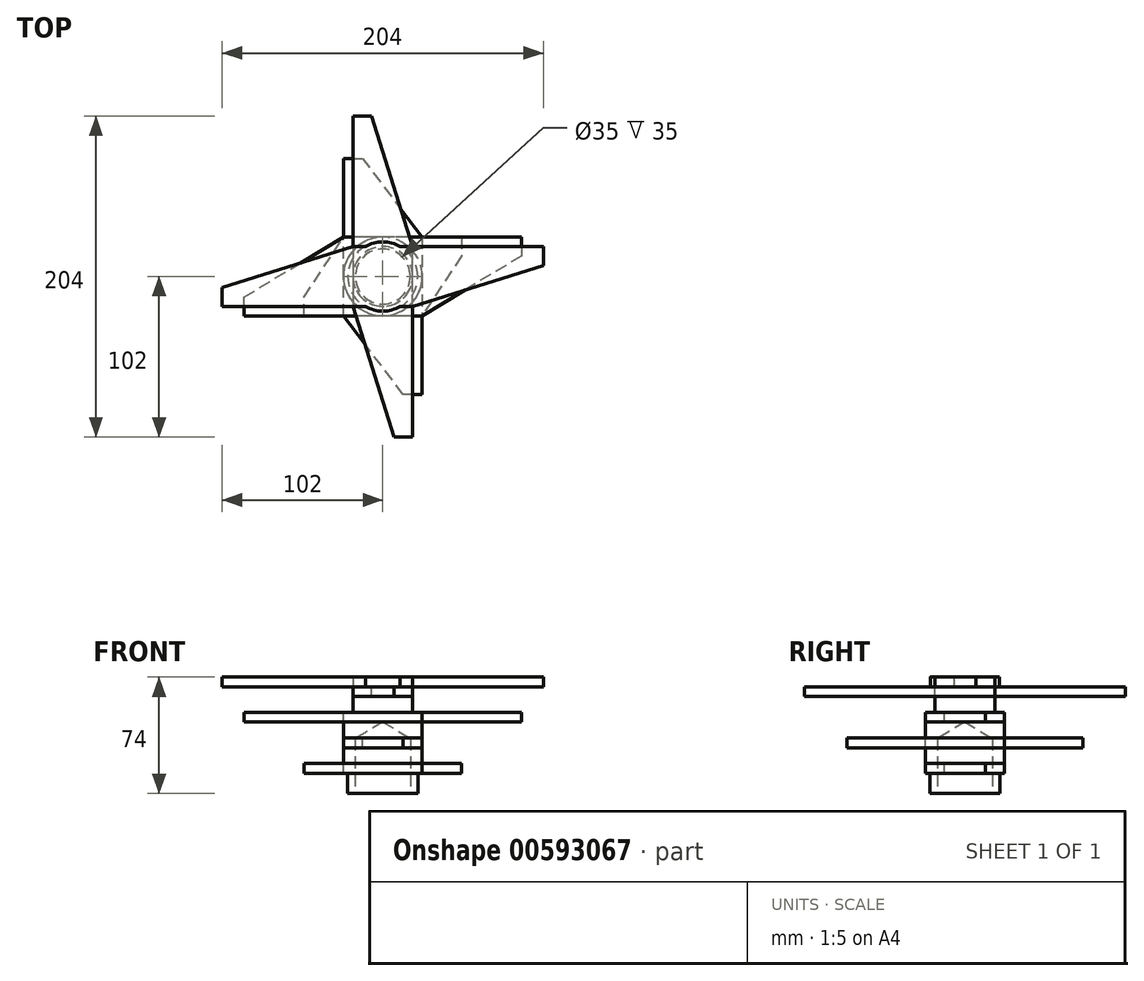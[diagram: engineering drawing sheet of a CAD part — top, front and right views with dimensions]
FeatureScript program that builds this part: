
annotation { "Feature Type Name" : "Feature", "Feature Type Description" : "" }
export const myFeature = defineFeature(function(context is Context, id is Id, definition is map)
    precondition{}
    {
        {
            var Q0;
            Q0=qCreatedBy(makeId("Top.planeOp"),FACE);
            var sketch = newSketch(context, id + "F0", { "sketchPlane" : qUnion([Q0])});
            skArc(sketch, "E0", {"start": v(11.1, 19) * mm, "mid": v(0, 22) * mm, "end": v(-11.1, 19) * mm});
            skLineSegment(sketch, "E1.bottom", {"start": v(19, -19) * mm, "end": v(11.1, -19) * mm});
            skLineSegment(sketch, "E2", {"start": v(102, 19) * mm, "end": v(102, 7) * mm});
            skLineSegment(sketch, "E3", {"start": v(102, 7) * mm, "end": v(19, -19) * mm});
            skLineSegment(sketch, "E4", {"start": v(-102, -19) * mm, "end": v(-102, -7) * mm});
            skLineSegment(sketch, "E5", {"start": v(-102, -7) * mm, "end": v(-19, 19) * mm});
            skLineSegment(sketch, "E6", {"start": v(-102, -19) * mm, "end": v(-11.1, -19) * mm});
            skLineSegment(sketch, "E7", {"start": v(11.1, -19) * mm, "end": v(19, -19) * mm});
            skLineSegment(sketch, "E8", {"start": v(-11.1, 19) * mm, "end": v(-19, 19) * mm});
            skPoint(sketch, "E9.orphan", {"position": v(0, 19) * mm});
            skArc(sketch, "E10.trimOffspring", {"start": v(-11.1, -19) * mm, "mid": v(0, -22) * mm, "end": v(11.1, -19) * mm});
            skPoint(sketch, "E11.orphan", {"position": v(0, -19) * mm});
            skLineSegment(sketch, "E12", {"start": v(11.1, 19) * mm, "end": v(102, 19) * mm});
            skSolve(sketch);
        }
        {
            var Q0;
            Q0=makeQuery(id+"F0.imprint","IMPRINT",FACE,{"disambiguationData":[TD([[makeQuery(id+"F0.imprint","IMPRINT",EDGE,{"derivedFrom":sQuery(id+"F0.wireOp",EDGE,"E0")}),1.0]])]});
            extrude(context, id + "F1", {"entities" : qUnion([Q0]), "depth" : 6.2 * mm, "offsetDistance" : 25 * mm});
        }
        {
            var Q0;
            Q0=makeQuery(id+"F1.opExtrude","CAP_FACE",FACE,{"disambiguationData":[OSD([sQuery(id+"F0.wireOp",EDGE,"E0"),sQuery(id+"F0.wireOp",EDGE,"E2"),sQuery(id+"F0.wireOp",EDGE,"E3"),sQuery(id+"F0.wireOp",EDGE,"E4"),sQuery(id+"F0.wireOp",EDGE,"E5"),sQuery(id+"F0.wireOp",EDGE,"E6"),sQuery(id+"F0.wireOp",EDGE,"E7"),sQuery(id+"F0.wireOp",EDGE,"E8"),sQuery(id+"F0.wireOp",EDGE,"E10.trimOffspring"),sQuery(id+"F0.wireOp",EDGE,"E12")])],"isStart":true});
            var sketch = newSketch(context, id + "F2", { "sketchPlane" : qUnion([Q0])});
            skLineSegment(sketch, "E13", {"start": v(-19, 0) * mm, "end": v(-19, 19) * mm});
            skLineSegment(sketch, "E14", {"start": v(19, 102) * mm, "end": v(19, 0) * mm});
            skLineSegment(sketch, "E15", {"start": v(19, 0) * mm, "end": v(19, -19) * mm});
            skLineSegment(sketch, "E16", {"start": v(-19, -102) * mm, "end": v(-19, 0) * mm});
            skLineSegment(sketch, "E17", {"start": v(19, 102) * mm, "end": v(7, 102) * mm});
            skLineSegment(sketch, "E18", {"start": v(7, 102) * mm, "end": v(-19, 19) * mm});
            skLineSegment(sketch, "E19", {"start": v(-19, -102) * mm, "end": v(-7, -102) * mm});
            skLineSegment(sketch, "E20", {"start": v(-7, -102) * mm, "end": v(19, -19) * mm});
            skSolve(sketch);
        }
        {
            var Q0;
            {var subQ5=sQuery(id+"F2.wireOp",EDGE,"E13");Q0=makeQuery(id+"F2.imprint","IMPRINT",FACE,{"disambiguationData":[TD([[makeQuery(id+"F2.imprint","IMPRINT",EDGE,{"derivedFrom":subQ5}),-1.0]])]});}
            var Q1;
            {var subQ3=sQuery(id+"F2.wireOp",EDGE,"E19");Q1=makeQuery(id+"F2.imprint","IMPRINT",FACE,{"disambiguationData":[TD([[makeQuery(id+"F2.imprint","IMPRINT",EDGE,{"derivedFrom":subQ3}),1.0]])]});}
            var Q2;
            {var subQ2=sQuery(id+"F2.wireOp",EDGE,"E17");Q2=makeQuery(id+"F2.imprint","IMPRINT",FACE,{"disambiguationData":[TD([[makeQuery(id+"F2.imprint","IMPRINT",EDGE,{"derivedFrom":subQ2}),1.0]])]});}
            extrude(context, id + "F3", {"entities" : qUnion([Q0, Q1, Q2]), "operationType" : NewBodyOperationType.ADD, "depth" : 6.2 * mm, "offsetDistance" : 25 * mm});
        }
        {
            var Q0;
            Q0=makeQuery(id+"F3.opExtrude","CAP_FACE",FACE,{"disambiguationData":[OSD([sQuery(id+"F2.wireOp",EDGE,"E13"),sQuery(id+"F2.wireOp",EDGE,"E14"),sQuery(id+"F2.wireOp",EDGE,"E15"),sQuery(id+"F2.wireOp",EDGE,"E16"),sQuery(id+"F2.wireOp",EDGE,"E17"),sQuery(id+"F2.wireOp",EDGE,"E18"),sQuery(id+"F2.wireOp",EDGE,"E19"),sQuery(id+"F2.wireOp",EDGE,"E20")])],"isStart":false});
            var sketch = newSketch(context, id + "F4", { "sketchPlane" : qUnion([Q0])});
            skCircle(sketch, "E21", {"center": v(0, 0) * mm, "radius": 19 * mm});
            skSolve(sketch);
        }
        {
            var Q0;
            {var subQ0=sQuery(id+"F4.wireOp",EDGE,"E21");var subQ3=makeQuery(id+"F3.opExtrude","CAP_EDGE",EDGE,{"disambiguationData":[OSD([sQuery(id+"F2.wireOp",EDGE,"E20")])],"isStart":false});var subQ4=makeQuery(id+"F4.imprint","INTERSECT",VERTEX,{"derivedFrom":[subQ3,subQ0]});Q0=makeQuery(id+"F4.imprint","IMPRINT",FACE,{"disambiguationData":[TD([[makeQuery(id+"F4.imprint","IMPRINT",EDGE,{"disambiguationData":[TD([[subQ4,-1.0]])],"derivedFrom":subQ0}),1.0]])]});}
            var Q1;
            {var subQ3=sQuery(id+"F4.wireOp",EDGE,"E21");var subQ5=makeQuery(id+"F3.opExtrude","CAP_EDGE",EDGE,{"disambiguationData":[OSD([sQuery(id+"F2.wireOp",EDGE,"E18")])],"isStart":false});var subQ10=makeQuery(id+"F4.imprint","INTERSECT",VERTEX,{"derivedFrom":[subQ5,subQ3]});Q1=makeQuery(id+"F4.imprint","IMPRINT",FACE,{"disambiguationData":[TD([[makeQuery(id+"F4.imprint","IMPRINT",EDGE,{"disambiguationData":[TD([[subQ10,1.0]])],"derivedFrom":subQ3}),1.0]])]});}
            var Q2;
            {var subQ0=sQuery(id+"F4.wireOp",EDGE,"E21");var subQ1=makeQuery(id+"F3.opExtrude","CAP_EDGE",EDGE,{"disambiguationData":[OSD([sQuery(id+"F2.wireOp",EDGE,"E18")])],"isStart":false});var subQ2=makeQuery(id+"F4.imprint","INTERSECT",VERTEX,{"derivedFrom":[subQ1,subQ0]});Q2=makeQuery(id+"F4.imprint","IMPRINT",FACE,{"disambiguationData":[TD([[makeQuery(id+"F4.imprint","IMPRINT",EDGE,{"disambiguationData":[TD([[subQ2,-1.0]])],"derivedFrom":subQ0}),1.0]])]});}
            extrude(context, id + "F5", {"entities" : qUnion([Q0, Q1, Q2]), "operationType" : NewBodyOperationType.ADD, "depth" : 10 * mm, "offsetDistance" : 25 * mm});
        }
        {
            var Q0;
            Q0=makeQuery(id+"F5.opExtrude","CAP_FACE",FACE,{"disambiguationData":[OSD([sQuery(id+"F4.wireOp",EDGE,"E21")])],"isStart":false});
            var sketch = newSketch(context, id + "F6", { "sketchPlane" : qUnion([Q0])});
            skLineSegment(sketch, "E22.bottom", {"start": v(25, -25) * mm, "end": v(-25, -25) * mm});
            skLineSegment(sketch, "E22.top", {"start": v(25, 25) * mm, "end": v(-25, 25) * mm});
            skLineSegment(sketch, "E22.left", {"start": v(25, -25) * mm, "end": v(25, 25) * mm});
            skLineSegment(sketch, "E22.right", {"start": v(-25, -25) * mm, "end": v(-25, 25) * mm});
            skPoint(sketch, "E22.middle", {"position": v(0, 0) * mm});
            skLineSegment(sketch, "E23", {"start": v(25, -25) * mm, "end": v(88, -25) * mm});
            skLineSegment(sketch, "E24", {"start": v(88, -25) * mm, "end": v(88, -13) * mm});
            skLineSegment(sketch, "E25", {"start": v(88, -13) * mm, "end": v(25, 25) * mm});
            skLineSegment(sketch, "E26", {"start": v(-25, 25) * mm, "end": v(-88, 25) * mm});
            skLineSegment(sketch, "E27", {"start": v(-88, 25) * mm, "end": v(-88, 13) * mm});
            skLineSegment(sketch, "E28", {"start": v(-88, 13) * mm, "end": v(-25, -25) * mm});
            skSolve(sketch);
        }
        {
            var Q0;
            Q0=makeQuery(id+"F6.imprint","IMPRINT",FACE,{"disambiguationData":[TD([[makeQuery(id+"F6.imprint","IMPRINT",EDGE,{"derivedFrom":sQuery(id+"F6.wireOp",EDGE,"E22.bottom")}),-1.0]])]});
            var Q1;
            Q1=makeQuery(id+"F6.imprint","IMPRINT",FACE,{"disambiguationData":[TD([[makeQuery(id+"F6.imprint","IMPRINT",EDGE,{"derivedFrom":sQuery(id+"F6.wireOp",EDGE,"E22.left")}),-1.0]])]});
            var Q2;
            Q2=makeQuery(id+"F6.imprint","IMPRINT",FACE,{"disambiguationData":[TD([[makeQuery(id+"F6.imprint","IMPRINT",EDGE,{"derivedFrom":sQuery(id+"F6.wireOp",EDGE,"E22.right")}),1.0]])]});
            var Q3;
            Q3=makeQuery(id+"F6.imprint","IMPRINT",FACE,{"disambiguationData":[TD([[makeQuery(id+"F6.imprint","IMPRINT",EDGE,{"derivedFrom":makeQuery(id+"F5.opExtrude","CAP_EDGE",EDGE,{"disambiguationData":[OSD([sQuery(id+"F4.wireOp",EDGE,"E21")])],"isStart":false})}),1.0]])]});
            extrude(context, id + "F7", {"entities" : qUnion([Q0, Q1, Q2, Q3]), "operationType" : NewBodyOperationType.ADD, "depth" : 6.2 * mm, "offsetDistance" : 25 * mm});
        }
        {
            var Q0;
            Q0=makeQuery(id+"F7.opExtrude","CAP_FACE",FACE,{"disambiguationData":[OSD([sQuery(id+"F6.wireOp",EDGE,"E22.bottom"),sQuery(id+"F6.wireOp",EDGE,"E22.top"),sQuery(id+"F6.wireOp",EDGE,"E23"),sQuery(id+"F6.wireOp",EDGE,"E24"),sQuery(id+"F6.wireOp",EDGE,"E25"),sQuery(id+"F6.wireOp",EDGE,"E26"),sQuery(id+"F6.wireOp",EDGE,"E27"),sQuery(id+"F6.wireOp",EDGE,"E28")])],"isStart":false});
            var sketch = newSketch(context, id + "F8", { "sketchPlane" : qUnion([Q0])});
            skCircle(sketch, "E29", {"center": v(0, 0) * mm, "radius": 25 * mm});
            skSolve(sketch);
        }
        {
            var Q0;
            {var subQ0=sQuery(id+"F8.wireOp",EDGE,"E29");var subQ1=makeQuery(id+"F8.imprint","INTERSECT",VERTEX,{"derivedFrom":[makeQuery(id+"F7.opExtrude","CAP_EDGE",EDGE,{"disambiguationData":[OSD([sQuery(id+"F6.wireOp",EDGE,"E22.bottom"),sQuery(id+"F6.wireOp",EDGE,"E23")])],"isStart":false}),subQ0]});Q0=makeQuery(id+"F8.imprint","IMPRINT",FACE,{"disambiguationData":[TD([[makeQuery(id+"F8.imprint","IMPRINT",EDGE,{"disambiguationData":[TD([[subQ1,1.0]])],"derivedFrom":subQ0}),1.0]])]});}
            extrude(context, id + "F9", {"entities" : qUnion([Q0]), "operationType" : NewBodyOperationType.ADD, "depth" : 10 * mm, "offsetDistance" : 25 * mm});
        }
        {
            var Q0;
            Q0=makeQuery(id+"F9.opExtrude","CAP_FACE",FACE,{"disambiguationData":[OSD([sQuery(id+"F8.wireOp",EDGE,"E29")])],"isStart":false});
            var sketch = newSketch(context, id + "F10", { "sketchPlane" : qUnion([Q0])});
            skLineSegment(sketch, "E30.bottom", {"start": v(-25, -25) * mm, "end": v(25, -25) * mm});
            skLineSegment(sketch, "E30.top", {"start": v(-25, 25) * mm, "end": v(25, 25) * mm});
            skLineSegment(sketch, "E30.left", {"start": v(-25, -25) * mm, "end": v(-25, 25) * mm});
            skLineSegment(sketch, "E30.right", {"start": v(25, -25) * mm, "end": v(25, 25) * mm});
            skPoint(sketch, "E30.middle", {"position": v(0, 0) * mm});
            skLineSegment(sketch, "E31", {"start": v(25, 25) * mm, "end": v(25, 75) * mm});
            skLineSegment(sketch, "E32", {"start": v(25, 75) * mm, "end": v(13, 75) * mm});
            skLineSegment(sketch, "E33", {"start": v(13, 75) * mm, "end": v(-25, 25) * mm});
            skLineSegment(sketch, "E34", {"start": v(-25, -75) * mm, "end": v(-13, -75) * mm});
            skLineSegment(sketch, "E35", {"start": v(-13, -75) * mm, "end": v(25, -25) * mm});
            skLineSegment(sketch, "E36", {"start": v(-25, -25) * mm, "end": v(-25, -75) * mm});
            skSolve(sketch);
        }
        {
            var Q0;
            {var subQ0=sQuery(id+"F10.wireOp",EDGE,"E31");Q0=makeQuery(id+"F10.imprint","IMPRINT",FACE,{"disambiguationData":[TD([[makeQuery(id+"F10.imprint","IMPRINT",EDGE,{"derivedFrom":subQ0}),1.0]])]});}
            var Q1;
            {var subQ0=sQuery(id+"F10.wireOp",EDGE,"E30.right");var subQ3=makeQuery(id+"F9.opExtrude","CAP_EDGE",EDGE,{"disambiguationData":[OSD([sQuery(id+"F8.wireOp",EDGE,"E29")])],"isStart":false});var subQ5=makeQuery(id+"F10.imprint","INTERSECT",VERTEX,{"derivedFrom":[subQ3,subQ0]});Q1=makeQuery(id+"F10.imprint","IMPRINT",FACE,{"disambiguationData":[TD([[makeQuery(id+"F10.imprint","IMPRINT",EDGE,{"disambiguationData":[TD([[subQ5,-1.0]])],"derivedFrom":subQ3}),-1.0]])]});}
            var Q2;
            {var subQ0=makeQuery(id+"F9.opExtrude","CAP_EDGE",EDGE,{"disambiguationData":[OSD([sQuery(id+"F8.wireOp",EDGE,"E29")])],"isStart":false});var subQ1=makeQuery(id+"F10.imprint","INTERSECT",VERTEX,{"derivedFrom":[subQ0,sQuery(id+"F10.wireOp",EDGE,"E30.left")]});Q2=makeQuery(id+"F10.imprint","IMPRINT",FACE,{"disambiguationData":[TD([[makeQuery(id+"F10.imprint","IMPRINT",EDGE,{"disambiguationData":[TD([[subQ1,-1.0]])],"derivedFrom":subQ0}),1.0]])]});}
            var Q3;
            {var subQ0=sQuery(id+"F10.wireOp",EDGE,"E30.right");var subQ3=makeQuery(id+"F9.opExtrude","CAP_EDGE",EDGE,{"disambiguationData":[OSD([sQuery(id+"F8.wireOp",EDGE,"E29")])],"isStart":false});var subQ5=makeQuery(id+"F10.imprint","INTERSECT",VERTEX,{"derivedFrom":[subQ3,subQ0]});Q3=makeQuery(id+"F10.imprint","IMPRINT",FACE,{"disambiguationData":[TD([[makeQuery(id+"F10.imprint","IMPRINT",EDGE,{"disambiguationData":[TD([[subQ5,1.0]])],"derivedFrom":subQ3}),-1.0]])]});}
            var Q4;
            Q4=makeQuery(id+"F10.imprint","IMPRINT",FACE,{"disambiguationData":[TD([[makeQuery(id+"F10.imprint","IMPRINT",EDGE,{"derivedFrom":sQuery(id+"F10.wireOp",EDGE,"E34")}),1.0]])]});
            var Q5;
            {var subQ0=sQuery(id+"F10.wireOp",EDGE,"E30.left");var subQ3=makeQuery(id+"F9.opExtrude","CAP_EDGE",EDGE,{"disambiguationData":[OSD([sQuery(id+"F8.wireOp",EDGE,"E29")])],"isStart":false});var subQ5=makeQuery(id+"F10.imprint","INTERSECT",VERTEX,{"derivedFrom":[subQ3,subQ0]});Q5=makeQuery(id+"F10.imprint","IMPRINT",FACE,{"disambiguationData":[TD([[makeQuery(id+"F10.imprint","IMPRINT",EDGE,{"disambiguationData":[TD([[subQ5,-1.0]])],"derivedFrom":subQ3}),-1.0]])]});}
            var Q6;
            {var subQ0=sQuery(id+"F10.wireOp",EDGE,"E30.left");var subQ3=makeQuery(id+"F9.opExtrude","CAP_EDGE",EDGE,{"disambiguationData":[OSD([sQuery(id+"F8.wireOp",EDGE,"E29")])],"isStart":false});var subQ5=makeQuery(id+"F10.imprint","INTERSECT",VERTEX,{"derivedFrom":[subQ3,subQ0]});Q6=makeQuery(id+"F10.imprint","IMPRINT",FACE,{"disambiguationData":[TD([[makeQuery(id+"F10.imprint","IMPRINT",EDGE,{"disambiguationData":[TD([[subQ5,1.0]])],"derivedFrom":subQ3}),-1.0]])]});}
            extrude(context, id + "F11", {"entities" : qUnion([Q0, Q1, Q2, Q3, Q4, Q5, Q6]), "operationType" : NewBodyOperationType.ADD, "depth" : 6.2 * mm, "offsetDistance" : 25 * mm});
        }
        {
            var Q0;
            Q0=makeQuery(id+"F11.opExtrude","CAP_FACE",FACE,{"disambiguationData":[OSD([sQuery(id+"F10.wireOp",EDGE,"E30.left"),sQuery(id+"F10.wireOp",EDGE,"E30.right"),sQuery(id+"F10.wireOp",EDGE,"E31"),sQuery(id+"F10.wireOp",EDGE,"E32"),sQuery(id+"F10.wireOp",EDGE,"E33"),sQuery(id+"F10.wireOp",EDGE,"E34"),sQuery(id+"F10.wireOp",EDGE,"E35"),sQuery(id+"F10.wireOp",EDGE,"E36")])],"isStart":false});
            var sketch = newSketch(context, id + "F12", { "sketchPlane" : qUnion([Q0])});
            skCircle(sketch, "E37", {"center": v(0, 0) * mm, "radius": 25 * mm});
            skSolve(sketch);
        }
        {
            var Q0;
            {var subQ0=sQuery(id+"F12.wireOp",EDGE,"E37");var subQ1=makeQuery(id+"F12.imprint","INTERSECT",VERTEX,{"derivedFrom":[makeQuery(id+"F11.opExtrude","CAP_EDGE",EDGE,{"disambiguationData":[OSD([sQuery(id+"F10.wireOp",EDGE,"E30.left"),sQuery(id+"F10.wireOp",EDGE,"E36")])],"isStart":false}),subQ0]});Q0=makeQuery(id+"F12.imprint","IMPRINT",FACE,{"disambiguationData":[TD([[makeQuery(id+"F12.imprint","IMPRINT",EDGE,{"disambiguationData":[TD([[subQ1,1.0]])],"derivedFrom":subQ0}),1.0]])]});}
            extrude(context, id + "F13", {"entities" : qUnion([Q0]), "operationType" : NewBodyOperationType.ADD, "depth" : 10 * mm, "offsetDistance" : 25 * mm});
        }
        {
            var Q0;
            Q0=makeQuery(id+"F13.opExtrude","CAP_FACE",FACE,{"disambiguationData":[OSD([sQuery(id+"F12.wireOp",EDGE,"E37")])],"isStart":false});
            var sketch = newSketch(context, id + "F14", { "sketchPlane" : qUnion([Q0])});
            skLineSegment(sketch, "E38.bottom", {"start": v(25, -25) * mm, "end": v(-25, -25) * mm});
            skLineSegment(sketch, "E38.top", {"start": v(25, 25) * mm, "end": v(-25, 25) * mm});
            skLineSegment(sketch, "E38.left", {"start": v(25, -25) * mm, "end": v(25, 25) * mm});
            skLineSegment(sketch, "E38.right", {"start": v(-25, -25) * mm, "end": v(-25, 25) * mm});
            skPoint(sketch, "E38.middle", {"position": v(0, 0) * mm});
            skLineSegment(sketch, "E39", {"start": v(25, -25) * mm, "end": v(50, -25) * mm});
            skLineSegment(sketch, "E40", {"start": v(50, -25) * mm, "end": v(50, -13) * mm});
            skLineSegment(sketch, "E41", {"start": v(50, -13) * mm, "end": v(25, 25) * mm});
            skLineSegment(sketch, "E42", {"start": v(-25, 25) * mm, "end": v(-50, 25) * mm});
            skLineSegment(sketch, "E43", {"start": v(-50, 25) * mm, "end": v(-50, 13) * mm});
            skLineSegment(sketch, "E44", {"start": v(-50, 13) * mm, "end": v(-25, -25) * mm});
            skSolve(sketch);
        }
        {
            var Q0;
            {var subQ0=makeQuery(id+"F13.opExtrude","CAP_EDGE",EDGE,{"disambiguationData":[OSD([sQuery(id+"F12.wireOp",EDGE,"E37")])],"isStart":false});var subQ1=makeQuery(id+"F14.imprint","INTERSECT",VERTEX,{"derivedFrom":[subQ0,sQuery(id+"F14.wireOp",EDGE,"E38.bottom")]});Q0=makeQuery(id+"F14.imprint","IMPRINT",FACE,{"disambiguationData":[TD([[makeQuery(id+"F14.imprint","IMPRINT",EDGE,{"disambiguationData":[TD([[subQ1,-1.0]])],"derivedFrom":subQ0}),1.0]])]});}
            var Q1;
            {var subQ1=sQuery(id+"F14.wireOp",EDGE,"E38.top");var subQ3=makeQuery(id+"F13.opExtrude","CAP_EDGE",EDGE,{"disambiguationData":[OSD([sQuery(id+"F12.wireOp",EDGE,"E37")])],"isStart":false});var subQ4=makeQuery(id+"F14.imprint","INTERSECT",VERTEX,{"derivedFrom":[subQ3,subQ1]});Q1=makeQuery(id+"F14.imprint","IMPRINT",FACE,{"disambiguationData":[TD([[makeQuery(id+"F14.imprint","IMPRINT",EDGE,{"disambiguationData":[TD([[subQ4,1.0]])],"derivedFrom":subQ3}),-1.0]])]});}
            var Q2;
            {var subQ1=sQuery(id+"F14.wireOp",EDGE,"E38.bottom");var subQ3=makeQuery(id+"F13.opExtrude","CAP_EDGE",EDGE,{"disambiguationData":[OSD([sQuery(id+"F12.wireOp",EDGE,"E37")])],"isStart":false});var subQ4=makeQuery(id+"F14.imprint","INTERSECT",VERTEX,{"derivedFrom":[subQ3,subQ1]});Q2=makeQuery(id+"F14.imprint","IMPRINT",FACE,{"disambiguationData":[TD([[makeQuery(id+"F14.imprint","IMPRINT",EDGE,{"disambiguationData":[TD([[subQ4,-1.0]])],"derivedFrom":subQ3}),-1.0]])]});}
            var Q3;
            {var subQ1=sQuery(id+"F14.wireOp",EDGE,"E38.bottom");var subQ3=makeQuery(id+"F13.opExtrude","CAP_EDGE",EDGE,{"disambiguationData":[OSD([sQuery(id+"F12.wireOp",EDGE,"E37")])],"isStart":false});var subQ4=makeQuery(id+"F14.imprint","INTERSECT",VERTEX,{"derivedFrom":[subQ3,subQ1]});Q3=makeQuery(id+"F14.imprint","IMPRINT",FACE,{"disambiguationData":[TD([[makeQuery(id+"F14.imprint","IMPRINT",EDGE,{"disambiguationData":[TD([[subQ4,1.0]])],"derivedFrom":subQ3}),-1.0]])]});}
            var Q4;
            {var subQ1=sQuery(id+"F14.wireOp",EDGE,"E38.top");var subQ3=makeQuery(id+"F13.opExtrude","CAP_EDGE",EDGE,{"disambiguationData":[OSD([sQuery(id+"F12.wireOp",EDGE,"E37")])],"isStart":false});var subQ4=makeQuery(id+"F14.imprint","INTERSECT",VERTEX,{"derivedFrom":[subQ3,subQ1]});Q4=makeQuery(id+"F14.imprint","IMPRINT",FACE,{"disambiguationData":[TD([[makeQuery(id+"F14.imprint","IMPRINT",EDGE,{"disambiguationData":[TD([[subQ4,-1.0]])],"derivedFrom":subQ3}),-1.0]])]});}
            var Q5;
            {var subQ0=sQuery(id+"F14.wireOp",EDGE,"E42");Q5=makeQuery(id+"F14.imprint","IMPRINT",FACE,{"disambiguationData":[TD([[makeQuery(id+"F14.imprint","IMPRINT",EDGE,{"derivedFrom":subQ0}),1.0]])]});}
            var Q6;
            {var subQ0=sQuery(id+"F14.wireOp",EDGE,"E39");Q6=makeQuery(id+"F14.imprint","IMPRINT",FACE,{"disambiguationData":[TD([[makeQuery(id+"F14.imprint","IMPRINT",EDGE,{"derivedFrom":subQ0}),1.0]])]});}
            extrude(context, id + "F15", {"entities" : qUnion([Q0, Q1, Q2, Q3, Q4, Q5, Q6]), "operationType" : NewBodyOperationType.ADD, "depth" : 6.2 * mm, "offsetDistance" : 25 * mm});
        }
        {
            var Q0;
            Q0=makeQuery(id+"F15.opExtrude","CAP_FACE",FACE,{"disambiguationData":[OSD([sQuery(id+"F14.wireOp",EDGE,"E38.bottom"),sQuery(id+"F14.wireOp",EDGE,"E38.top"),sQuery(id+"F14.wireOp",EDGE,"E39"),sQuery(id+"F14.wireOp",EDGE,"E40"),sQuery(id+"F14.wireOp",EDGE,"E41"),sQuery(id+"F14.wireOp",EDGE,"E42"),sQuery(id+"F14.wireOp",EDGE,"E43"),sQuery(id+"F14.wireOp",EDGE,"E44")])],"isStart":false});
            var sketch = newSketch(context, id + "F16", { "sketchPlane" : qUnion([Q0])});
            skCircle(sketch, "E45", {"center": v(0, 0) * mm, "radius": 22.25 * mm});
            skSolve(sketch);
        }
        {
            var Q0;
            Q0=makeQuery(id+"F16.imprint","IMPRINT",FACE,{"disambiguationData":[TD([[makeQuery(id+"F16.imprint","IMPRINT",EDGE,{"derivedFrom":sQuery(id+"F16.wireOp",EDGE,"E45")}),1.0]])]});
            extrude(context, id + "F17", {"entities" : qUnion([Q0]), "operationType" : NewBodyOperationType.ADD, "depth" : 13 * mm, "offsetDistance" : 25 * mm});
        }
        {
            var Q0;
            Q0=makeQuery(id+"F17.opExtrude","CAP_FACE",FACE,{"disambiguationData":[OSD([sQuery(id+"F16.wireOp",EDGE,"E45")])],"isStart":false});
            var sketch = newSketch(context, id + "F18", { "sketchPlane" : qUnion([Q0])});
            skPoint(sketch, "E46", {"position": v(0, 0) * mm});
            skSolve(sketch);
        }
        {
            var Q0;
            Q0=sQuery(id+"F18.wireOp",VERTEX,"E46");
            var Q1;
            Q1=makeQuery(id+"F1.opExtrude","SWEPT_BODY",BODY,{"disambiguationData":[OSD([sQuery(id+"F0.wireOp",EDGE,"E0"),sQuery(id+"F0.wireOp",EDGE,"E2"),sQuery(id+"F0.wireOp",EDGE,"E3"),sQuery(id+"F0.wireOp",EDGE,"E4"),sQuery(id+"F0.wireOp",EDGE,"E5"),sQuery(id+"F0.wireOp",EDGE,"E6"),sQuery(id+"F0.wireOp",EDGE,"E7"),sQuery(id+"F0.wireOp",EDGE,"E8"),sQuery(id+"F0.wireOp",EDGE,"E10.trimOffspring"),sQuery(id+"F0.wireOp",EDGE,"E12")])]});
            hole(context, id + "F19", {"style" : HoleStyle.SIMPLE, "endStyle" : HoleEndStyle.BLIND, "holeDiameter" : 35 * mm, "majorDiameter" : 5 * mm, "holeDepth" : 35 * mm, "isTappedThrough" : true, "tappedDepth" : 12 * mm, "tapClearance" : 3, "startFromSketch" : true, "locations" : qUnion([Q0]), "scope" : qUnion([Q1])});
        }
    });
